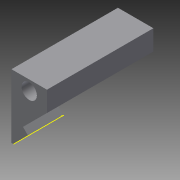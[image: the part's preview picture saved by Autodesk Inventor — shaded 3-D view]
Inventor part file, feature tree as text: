
AUTODESK INVENTOR PART (.ipt)
format: ipt  version: 2013 (Build 170138000, 138)  size: 119,296 bytes
history: native  units: mm
features: sketch x6, extrude x4, hole x3
ambient origin geometry x8: Origin, YZ Plane, XZ Plane, XY Plane, X Axis, Y Axis, Z Axis, Center Point
bodies: Solid1 (feature_tree)
feature tree (13):
  extrude  "Extrusion1"  Depth=20.0mm TaperAngle=0.0deg
  extrude  "Extrusion2"  Depth=5.1mm
  hole  "Hole1"  [1 undecoded]
  extrude  "Extrusion3"  Depth=1.0mm
  extrude  "Extrusion4"  Depth=1.0mm
  sketch  "Sketch6"  dims[d27=1.3mm d28=3.0mm d29=1.778mm d30=6.0mm d31=3.023mm d32=2.0mm d33=14.3117mm d34=8.0mm d35=20.594885mm d12=1.0mm d36=1.0mm d37=1.0mm]
  hole  "Hole2"  [1 undecoded]
  hole  "Hole3"  [1 undecoded]
  sketch  "Sketch1"  dims[d0=10.0mm d1=0.0mm d2=20.0mm d3=0.0mm]
  sketch  "Sketch2"  dims[d4=4.318mm d5=6.0mm d6=8.433mm d7=2.0mm d8=14.3117mm d9=31.0mm d10=20.594885mm d11=5.1mm]
  sketch  "Sketch3"  dims[d13=0.1mm d14=0.0mm d15=4.0mm]
  sketch  "Sketch4"  dims[d16=10.0mm d17=0.0mm]
  sketch  "Sketch5"  dims[d18=1.3mm d19=3.0mm d20=1.778mm d21=6.0mm d22=3.023mm d23=2.0mm d24=14.3117mm d25=8.0mm d26=20.594885mm]
note: 3 required parameter values undecoded (feature->parameter linkage not recoverable at this tier; creation-order binding heuristic only, values carry confidence <= 0.55)
